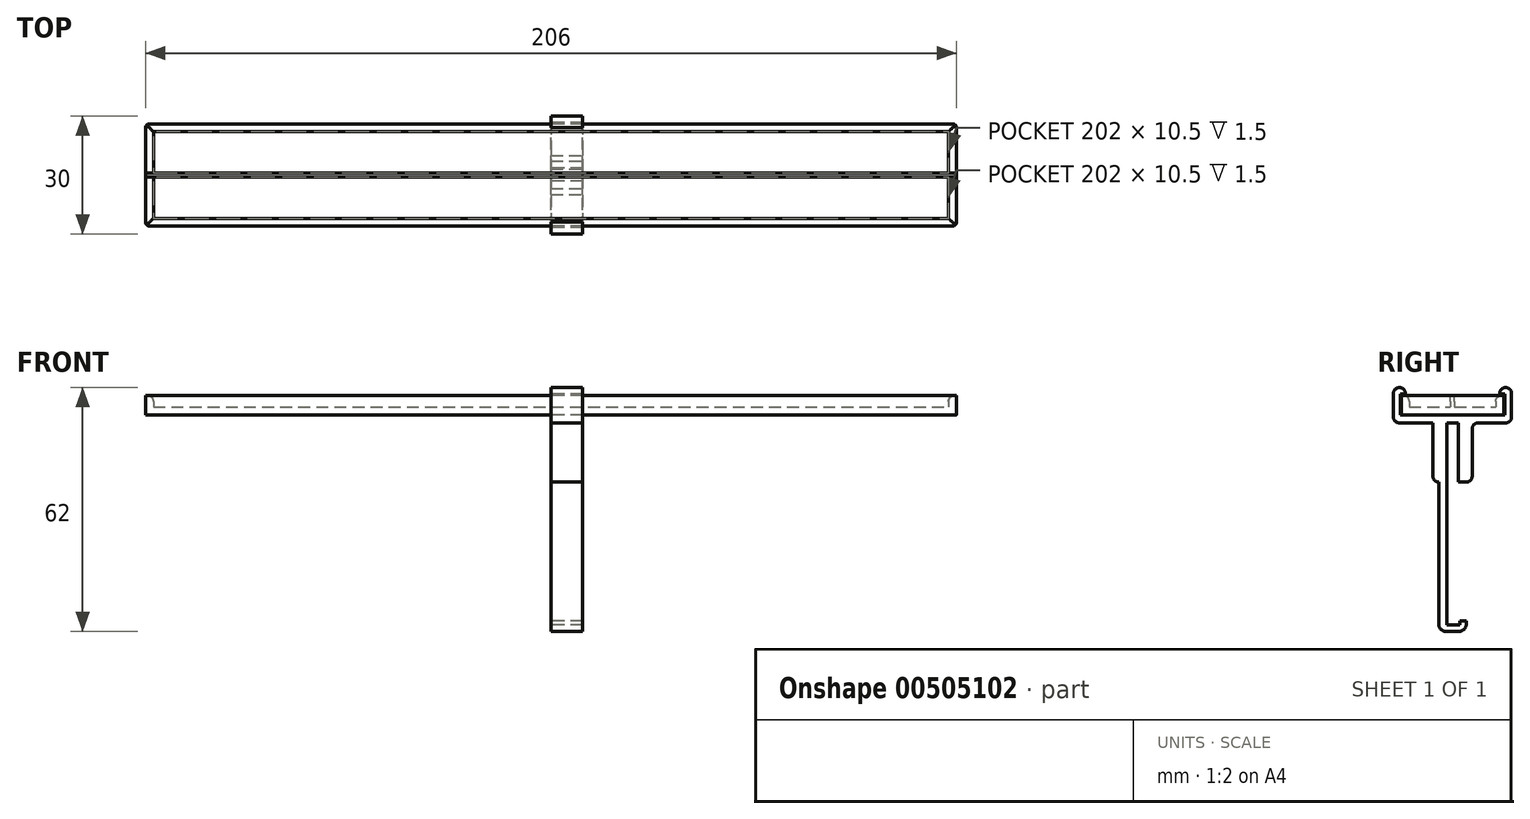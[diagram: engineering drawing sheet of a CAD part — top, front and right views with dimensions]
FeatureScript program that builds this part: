
annotation { "Feature Type Name" : "Feature", "Feature Type Description" : "" }
export const myFeature = defineFeature(function(context is Context, id is Id, definition is map)
    precondition{}
    {
        {
            var Q0;
            Q0=qCreatedBy(makeId("Top.planeOp"),FACE);
            var sketch = newSketch(context, id + "F0", { "sketchPlane" : qUnion([Q0])});
            skLineSegment(sketch, "E0.bottom", {"start": v(103, -13) * mm, "end": v(-103, -13) * mm});
            skLineSegment(sketch, "E0.top", {"start": v(103, 13) * mm, "end": v(-103, 13) * mm});
            skLineSegment(sketch, "E0.left", {"start": v(103, -13) * mm, "end": v(103, 13) * mm});
            skLineSegment(sketch, "E0.right", {"start": v(-103, -13) * mm, "end": v(-103, 13) * mm});
            skPoint(sketch, "E0.middle", {"position": v(0, 0) * mm});
            skSolve(sketch);
        }
        {
            var Q0;
            Q0 = qSketchRegion(id + "F0", true);
            extrude(context, id + "F1", {"entities" : qUnion([Q0]), "depth" : 2 * mm});
        }
        {
            var Q0;
            Q0=makeQuery(id+"F1.opExtrude","CAP_FACE",FACE,{"disambiguationData":[OSD([sQuery(id+"F0.wireOp",EDGE,"E0.bottom"),sQuery(id+"F0.wireOp",EDGE,"E0.top"),sQuery(id+"F0.wireOp",EDGE,"E0.left"),sQuery(id+"F0.wireOp",EDGE,"E0.right")])],"isStart":false});
            var sketch = newSketch(context, id + "F2", { "sketchPlane" : qUnion([Q0])});
            skLineSegment(sketch, "E1.0.0", {"start": v(103, -13) * mm, "end": v(103, 13) * mm});
            skLineSegment(sketch, "E1.0.1", {"start": v(103, 13) * mm, "end": v(-103, 13) * mm});
            skLineSegment(sketch, "E1.0.2", {"start": v(-103, 13) * mm, "end": v(-103, -13) * mm});
            skLineSegment(sketch, "E1.0.3", {"start": v(-103, -13) * mm, "end": v(103, -13) * mm});
            skLineSegment(sketch, "E2.0", {"start": v(101, 11) * mm, "end": v(-101, 11) * mm});
            skLineSegment(sketch, "E2.1", {"start": v(101, -11) * mm, "end": v(101, -0.5) * mm});
            skLineSegment(sketch, "E2.2", {"start": v(-101, -11) * mm, "end": v(101, -11) * mm});
            skLineSegment(sketch, "E2.3", {"start": v(-101, 11) * mm, "end": v(-101, 0.5) * mm});
            skPoint(sketch, "E3.middle", {"position": v(0, 0) * mm});
            skLineSegment(sketch, "E4.trimOffspring", {"start": v(-101, -0.5) * mm, "end": v(-101, -11) * mm});
            skLineSegment(sketch, "E5.trimOffspring", {"start": v(101, 0.5) * mm, "end": v(101, 11) * mm});
            skLineSegment(sketch, "E6", {"start": v(101, 0.5) * mm, "end": v(-101, 0.5) * mm});
            skLineSegment(sketch, "E7", {"start": v(-101, -0.5) * mm, "end": v(101, -0.5) * mm});
            skSolve(sketch);
        }
        {
            var Q0;
            Q0 = qSketchRegion(id + "F2", true);
            extrude(context, id + "F3", {"entities" : qUnion([Q0]), "operationType" : NewBodyOperationType.ADD, "depth" : 3 * mm});
        }
        {
            var Q0;
            Q0=makeQuery(id+"F3.opExtrude","CAP_EDGE",EDGE,{"disambiguationData":[OSD([sQuery(id+"F2.wireOp",EDGE,"E2.3")])],"isStart":false});
            var Q1;
            Q1=makeQuery(id+"F3.opExtrude","CAP_EDGE",EDGE,{"disambiguationData":[OSD([sQuery(id+"F2.wireOp",EDGE,"E2.0")])],"isStart":false});
            var Q2;
            Q2=makeQuery(id+"F3.opExtrude","CAP_EDGE",EDGE,{"disambiguationData":[OSD([sQuery(id+"F2.wireOp",EDGE,"E4.trimOffspring")])],"isStart":false});
            var Q3;
            Q3=makeQuery(id+"F3.opExtrude","CAP_EDGE",EDGE,{"disambiguationData":[OSD([sQuery(id+"F2.wireOp",EDGE,"E2.2")])],"isStart":false});
            var Q4;
            Q4=makeQuery(id+"F3.opExtrude","CAP_EDGE",EDGE,{"disambiguationData":[OSD([sQuery(id+"F2.wireOp",EDGE,"E5.trimOffspring")])],"isStart":false});
            var Q5;
            Q5=makeQuery(id+"F3.opExtrude","CAP_EDGE",EDGE,{"disambiguationData":[OSD([sQuery(id+"F2.wireOp",EDGE,"E2.1")])],"isStart":false});
            fillet(context, id + "F4", {"entities" : qUnion([Q0, Q1, Q2, Q3, Q4, Q5]), "radius" : 1.5 * mm, "tangentPropagation" : true, "allowEdgeOverflow" : false});
        }
        {
            var Q0;
            Q0=makeQuery(id+"F3.boolean.opBoolean","MERGE",EDGE,{"derivedFrom":[makeQuery(id+"F1.opExtrude","SWEPT_EDGE",EDGE,{"disambiguationData":[OSD([sQuery(id+"F0.wireOp",EDGE,"E0.top"),sQuery(id+"F0.wireOp",EDGE,"E0.left")])]}),makeQuery(id+"F3.opExtrude","SWEPT_EDGE",EDGE,{"disambiguationData":[OSD([sQuery(id+"F2.wireOp",EDGE,"E1.0.0"),sQuery(id+"F2.wireOp",EDGE,"E1.0.1")])]})]});
            var Q1;
            Q1=makeQuery(id+"F3.boolean.opBoolean","MERGE",EDGE,{"derivedFrom":[makeQuery(id+"F1.opExtrude","SWEPT_EDGE",EDGE,{"disambiguationData":[OSD([sQuery(id+"F0.wireOp",EDGE,"E0.bottom"),sQuery(id+"F0.wireOp",EDGE,"E0.left")])]}),makeQuery(id+"F3.opExtrude","SWEPT_EDGE",EDGE,{"disambiguationData":[OSD([sQuery(id+"F2.wireOp",EDGE,"E1.0.0"),sQuery(id+"F2.wireOp",EDGE,"E1.0.3")])]})]});
            var Q2;
            Q2=makeQuery(id+"F3.boolean.opBoolean","MERGE",EDGE,{"derivedFrom":[makeQuery(id+"F1.opExtrude","SWEPT_EDGE",EDGE,{"disambiguationData":[OSD([sQuery(id+"F0.wireOp",EDGE,"E0.bottom"),sQuery(id+"F0.wireOp",EDGE,"E0.right")])]}),makeQuery(id+"F3.opExtrude","SWEPT_EDGE",EDGE,{"disambiguationData":[OSD([sQuery(id+"F2.wireOp",EDGE,"E1.0.2"),sQuery(id+"F2.wireOp",EDGE,"E1.0.3")])]})]});
            var Q3;
            Q3=makeQuery(id+"F3.boolean.opBoolean","MERGE",EDGE,{"derivedFrom":[makeQuery(id+"F1.opExtrude","SWEPT_EDGE",EDGE,{"disambiguationData":[OSD([sQuery(id+"F0.wireOp",EDGE,"E0.top"),sQuery(id+"F0.wireOp",EDGE,"E0.right")])]}),makeQuery(id+"F3.opExtrude","SWEPT_EDGE",EDGE,{"disambiguationData":[OSD([sQuery(id+"F2.wireOp",EDGE,"E1.0.1"),sQuery(id+"F2.wireOp",EDGE,"E1.0.2")])]})]});
            fillet(context, id + "F5", {"entities" : qUnion([Q0, Q1, Q2, Q3]), "radius" : 1 * mm, "tangentPropagation" : true, "allowEdgeOverflow" : false});
        }
        {
            var Q0;
            Q0=qCreatedBy(makeId("Right.planeOp"),FACE);
            var sketch = newSketch(context, id + "F6", { "sketchPlane" : qUnion([Q0])});
            skLineSegment(sketch, "E8.0", {"start": v(12, 0) * mm, "end": v(13, 0) * mm});
            skLineSegment(sketch, "E9.0", {"start": v(-12, 0) * mm, "end": v(12, 0) * mm});
            skLineSegment(sketch, "E10.0", {"start": v(-13, 0) * mm, "end": v(-12, 0) * mm});
            skLineSegment(sketch, "E11.0", {"start": v(15, 7) * mm, "end": v(12, 7) * mm});
            skLineSegment(sketch, "E11.1", {"start": v(15, -2) * mm, "end": v(15, 7) * mm});
            skLineSegment(sketch, "E11.2", {"start": v(12, -2) * mm, "end": v(15, -2) * mm});
            skLineSegment(sketch, "E11.3", {"start": v(-12, 7) * mm, "end": v(-15, 7) * mm});
            skLineSegment(sketch, "E11.4", {"start": v(-15, 7) * mm, "end": v(-15, -2) * mm});
            skLineSegment(sketch, "E11.5", {"start": v(-15, -2) * mm, "end": v(-12, -2) * mm});
            skLineSegment(sketch, "E11.6", {"start": v(-12, -2) * mm, "end": v(12, -2) * mm});
            skLineSegment(sketch, "E12.0", {"start": v(13.3, 5.3) * mm, "end": v(13.3, 0) * mm});
            skLineSegment(sketch, "E12.1", {"start": v(12, 5.3) * mm, "end": v(13.3, 5.3) * mm});
            skLineSegment(sketch, "E13.0", {"start": v(-13.3, 5.3) * mm, "end": v(-12, 5.3) * mm});
            skLineSegment(sketch, "E13.1", {"start": v(-13.3, 0) * mm, "end": v(-13.3, 5.3) * mm});
            skLineSegment(sketch, "E14", {"start": v(-13.3, 0) * mm, "end": v(-13, 0) * mm});
            skLineSegment(sketch, "E15", {"start": v(13.3, 0) * mm, "end": v(13, 0) * mm});
            skLineSegment(sketch, "E16", {"start": v(12, 7) * mm, "end": v(12, 5.3) * mm});
            skLineSegment(sketch, "E17", {"start": v(-12, 7) * mm, "end": v(-12, 5.3) * mm});
            skSolve(sketch);
        }
        {
            var Q0;
            Q0 = qSketchRegion(id + "F6", true);
            extrude(context, id + "F7", {"entities" : qUnion([Q0]), "depth" : 8 * mm});
        }
        {
            var Q0;
            Q0=makeQuery(id+"F7.opExtrude","SWEPT_FACE",FACE,{"disambiguationData":[OSD([sQuery(id+"F6.wireOp",EDGE,"E11.2"),sQuery(id+"F6.wireOp",EDGE,"E11.5"),sQuery(id+"F6.wireOp",EDGE,"E11.6")])]});
            var sketch = newSketch(context, id + "F8", { "sketchPlane" : qUnion([Q0])});
            skLineSegment(sketch, "E18.bottom", {"start": v(0, 5) * mm, "end": v(8, 5) * mm});
            skLineSegment(sketch, "E18.top", {"start": v(0, -5) * mm, "end": v(8, -5) * mm});
            skLineSegment(sketch, "E18.left", {"start": v(0, 5) * mm, "end": v(0, 1.48) * mm});
            skLineSegment(sketch, "E18.right", {"start": v(8, 5) * mm, "end": v(8, 1.48) * mm});
            skLineSegment(sketch, "E19.bottom", {"start": v(0, 1.48) * mm, "end": v(8, 1.48) * mm});
            skLineSegment(sketch, "E19.top", {"start": v(0, -1.48) * mm, "end": v(8, -1.48) * mm});
            skLineSegment(sketch, "E20.trimOffspring", {"start": v(0, -1.47) * mm, "end": v(0, -5) * mm});
            skLineSegment(sketch, "E21.trimOffspring", {"start": v(8, -1.48) * mm, "end": v(8, -5) * mm});
            skSolve(sketch);
        }
        {
            var Q0;
            Q0 = qSketchRegion(id + "F8", true);
            extrude(context, id + "F9", {"entities" : qUnion([Q0]), "operationType" : NewBodyOperationType.ADD, "depth" : 15 * mm});
        }
        {
            var Q0;
            Q0=makeQuery(id+"F7.opExtrude","SWEPT_EDGE",EDGE,{"disambiguationData":[OSD([sQuery(id+"F6.wireOp",EDGE,"E11.3"),sQuery(id+"F6.wireOp",EDGE,"E11.4")])]});
            var Q1;
            Q1=makeQuery(id+"F7.opExtrude","SWEPT_EDGE",EDGE,{"disambiguationData":[OSD([sQuery(id+"F6.wireOp",EDGE,"E11.4"),sQuery(id+"F6.wireOp",EDGE,"E11.5")])]});
            var Q2;
            Q2=makeQuery(id+"F7.opExtrude","SWEPT_EDGE",EDGE,{"disambiguationData":[OSD([sQuery(id+"F6.wireOp",EDGE,"E11.3"),sQuery(id+"F6.wireOp",EDGE,"xxigbtJz-0GZ5-I3mQ-RcPI-NBe8b4R356NF")])]});
            var Q3;
            Q3=makeQuery(id+"F7.opExtrude","SWEPT_EDGE",EDGE,{"disambiguationData":[OSD([sQuery(id+"F6.wireOp",EDGE,"E11.0"),sQuery(id+"F6.wireOp",EDGE,"l1KlIqBO-z6LF-Rg04-zcvI-sIOI40xdQ3O2")])]});
            var Q4;
            Q4=makeQuery(id+"F7.opExtrude","SWEPT_EDGE",EDGE,{"disambiguationData":[OSD([sQuery(id+"F6.wireOp",EDGE,"E11.0"),sQuery(id+"F6.wireOp",EDGE,"E11.1")])]});
            var Q5;
            Q5=makeQuery(id+"F7.opExtrude","SWEPT_EDGE",EDGE,{"disambiguationData":[OSD([sQuery(id+"F6.wireOp",EDGE,"E11.1"),sQuery(id+"F6.wireOp",EDGE,"E11.2")])]});
            var Q6;
            Q6=makeQuery(id+"F9.opExtrude","CAP_EDGE",EDGE,{"disambiguationData":[OSD([sQuery(id+"F8.wireOp",EDGE,"E18.top")])],"isStart":true});
            var Q7;
            Q7=makeQuery(id+"F9.opExtrude","CAP_EDGE",EDGE,{"disambiguationData":[OSD([sQuery(id+"F8.wireOp",EDGE,"E18.bottom")])],"isStart":true});
            var Q8;
            Q8=makeQuery(id+"F9.opExtrude","CAP_EDGE",EDGE,{"disambiguationData":[OSD([sQuery(id+"F8.wireOp",EDGE,"E18.bottom")])],"isStart":false});
            var Q9;
            Q9=makeQuery(id+"F9.opExtrude","CAP_EDGE",EDGE,{"disambiguationData":[OSD([sQuery(id+"F8.wireOp",EDGE,"E18.top")])],"isStart":false});
            fillet(context, id + "F10", {"entities" : qUnion([Q0, Q1, Q2, Q3, Q4, Q5, Q6, Q7, Q8, Q9]), "radius" : 1.5 * mm, "tangentPropagation" : true, "allowEdgeOverflow" : false});
        }
        {
            var Q0;
            Q0=makeQuery(id+"F9.opExtrude","CAP_FACE",FACE,{"disambiguationData":[OSD([sQuery(id+"F8.wireOp",EDGE,"E18.bottom"),sQuery(id+"F8.wireOp",EDGE,"E18.left"),sQuery(id+"F8.wireOp",EDGE,"E18.right"),sQuery(id+"F8.wireOp",EDGE,"E19.bottom")])],"isStart":false});
            var sketch = newSketch(context, id + "F11", { "sketchPlane" : qUnion([Q0])});
            skLineSegment(sketch, "E22.0.0", {"start": v(8, 1.48) * mm, "end": v(8, 3.5) * mm});
            skLineSegment(sketch, "E22.0.1", {"start": v(8, 3.5) * mm, "end": v(0, 3.5) * mm});
            skLineSegment(sketch, "E22.0.2", {"start": v(0, 3.5) * mm, "end": v(0, 1.48) * mm});
            skLineSegment(sketch, "E22.0.3", {"start": v(0, 1.48) * mm, "end": v(8, 1.48) * mm});
            skSolve(sketch);
        }
        {
            var Q0;
            Q0 = qSketchRegion(id + "F11", true);
            extrude(context, id + "F12", {"entities" : qUnion([Q0]), "operationType" : NewBodyOperationType.ADD, "depth" : (50 - 17 + 2 + 3) * mm});
        }
        {
            var Q0;
            Q0=makeQuery(id+"F12.boolean.opBoolean","MERGE",FACE,{"derivedFrom":[makeQuery(id+"F9.opExtrude","SWEPT_FACE",FACE,{"disambiguationData":[OSD([sQuery(id+"F8.wireOp",EDGE,"E19.bottom")])]}),makeQuery(id+"F12.opExtrude","SWEPT_FACE",FACE,{"disambiguationData":[OSD([sQuery(id+"F11.wireOp",EDGE,"E22.0.3")])]})]});
            var sketch = newSketch(context, id + "F13", { "sketchPlane" : qUnion([Q0])});
            skLineSegment(sketch, "E23.bottom", {"start": v(-8, -55) * mm, "end": v(0, -55) * mm});
            skLineSegment(sketch, "E23.top", {"start": v(-8, -53.3) * mm, "end": v(0, -53.3) * mm});
            skLineSegment(sketch, "E23.left", {"start": v(-8, -55) * mm, "end": v(-8, -53.3) * mm});
            skLineSegment(sketch, "E23.right", {"start": v(0, -55) * mm, "end": v(0, -53.3) * mm});
            skSolve(sketch);
        }
        {
            var Q0;
            Q0 = qSketchRegion(id + "F13", true);
            extrude(context, id + "F14", {"entities" : qUnion([Q0]), "operationType" : NewBodyOperationType.ADD, "depth" : 5 * mm});
        }
        {
            var Q0;
            Q0=makeQuery(id+"F14.opExtrude","SWEPT_FACE",FACE,{"disambiguationData":[OSD([sQuery(id+"F13.wireOp",EDGE,"E23.top")])]});
            var sketch = newSketch(context, id + "F15", { "sketchPlane" : qUnion([Q0])});
            skLineSegment(sketch, "E24.bottom", {"start": v(8, 3.52) * mm, "end": v(0, 3.52) * mm});
            skLineSegment(sketch, "E24.top", {"start": v(8, 1.83) * mm, "end": v(0, 1.82) * mm});
            skLineSegment(sketch, "E24.left", {"start": v(8, 3.52) * mm, "end": v(8, 1.83) * mm});
            skLineSegment(sketch, "E24.right", {"start": v(0, 3.52) * mm, "end": v(0, 1.82) * mm});
            skSolve(sketch);
        }
        {
            var Q0;
            Q0 = qSketchRegion(id + "F15", true);
            extrude(context, id + "F16", {"entities" : qUnion([Q0]), "operationType" : NewBodyOperationType.ADD, "depth" : 1 * mm});
        }
        {
            var Q0;
            Q0=makeQuery(id+"F14.opExtrude","CAP_EDGE",EDGE,{"disambiguationData":[OSD([sQuery(id+"F13.wireOp",EDGE,"E23.bottom")])],"isStart":false});
            var Q1;
            Q1=makeQuery(id+"F12.opExtrude","CAP_EDGE",EDGE,{"disambiguationData":[OSD([sQuery(id+"F11.wireOp",EDGE,"E22.0.1")])],"isStart":false});
            fillet(context, id + "F17", {"entities" : qUnion([Q0, Q1]), "radius" : 2 * mm, "tangentPropagation" : true, "allowEdgeOverflow" : false});
        }
    });
